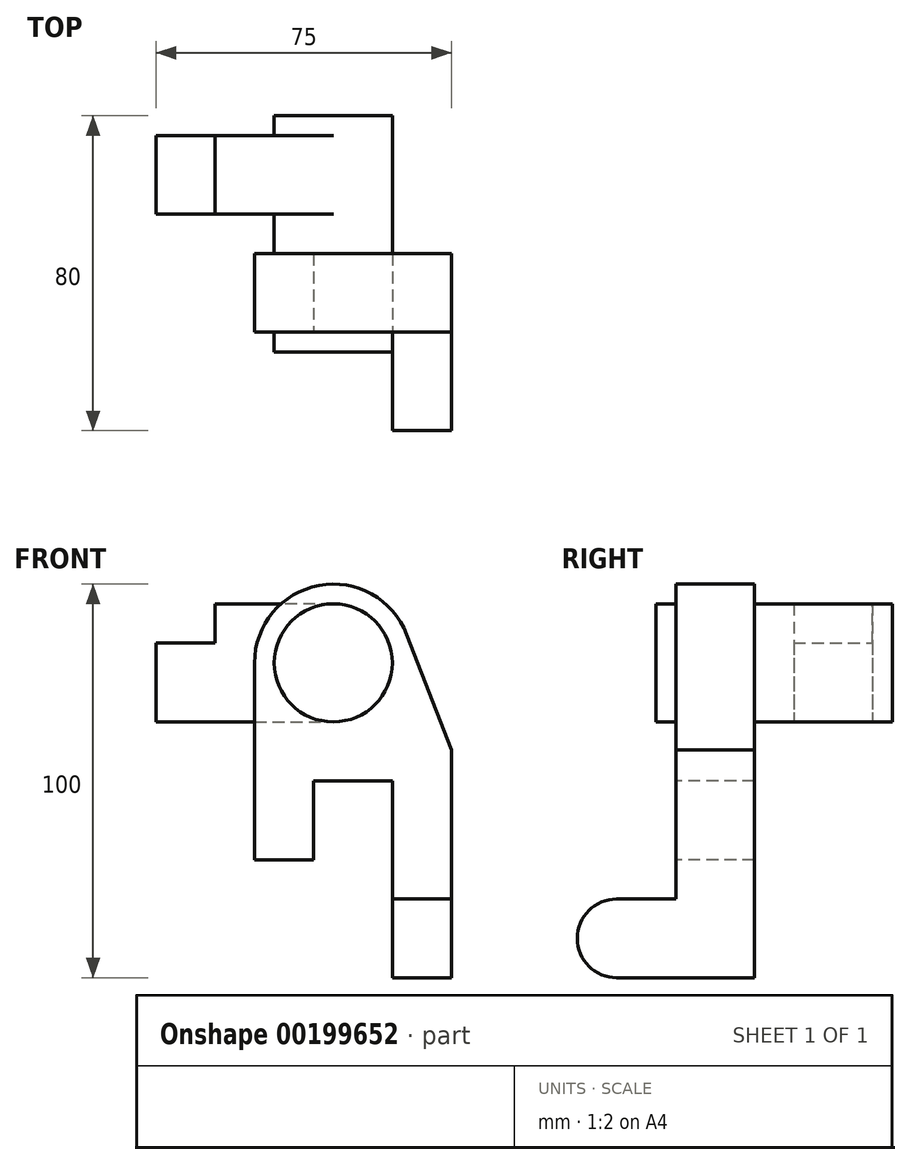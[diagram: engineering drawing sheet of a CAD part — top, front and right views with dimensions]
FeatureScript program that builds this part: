
annotation { "Feature Type Name" : "Feature", "Feature Type Description" : "" }
export const myFeature = defineFeature(function(context is Context, id is Id, definition is map)
    precondition{}
    {
        {
            var Q0;
            Q0=qCreatedBy(makeId("Front.planeOp"),FACE);
            var sketch = newSketch(context, id + "F0", { "sketchPlane" : qUnion([Q0])});
            skCircle(sketch, "E0", {"center": v(0, 0) * mm, "radius": 20 * mm});
            skLineSegment(sketch, "E1", {"start": v(-20, 0) * mm, "end": v(-20, -50) * mm});
            skLineSegment(sketch, "E2", {"start": v(-20, -50) * mm, "end": v(-5, -50) * mm});
            skLineSegment(sketch, "E3", {"start": v(-5, -50) * mm, "end": v(-5, -30) * mm});
            skLineSegment(sketch, "E4", {"start": v(-5, -30) * mm, "end": v(15, -30) * mm});
            skLineSegment(sketch, "E5", {"start": v(15, -30) * mm, "end": v(15, -80) * mm});
            skLineSegment(sketch, "E6", {"start": v(15, -80) * mm, "end": v(30, -80) * mm});
            skLineSegment(sketch, "E7", {"start": v(30, -80) * mm, "end": v(30, -22.08) * mm});
            skLineSegment(sketch, "E8", {"start": v(30, -22.08) * mm, "end": v(18.65, 7.22) * mm});
            skSolve(sketch);
        }
        {
            var Q0;
            {var subQ0=sQuery(id+"F0.wireOp",EDGE,"E1");Q0=makeQuery(id+"F0.imprint","IMPRINT",FACE,{"disambiguationData":[TD([[makeQuery(id+"F0.imprint","IMPRINT",EDGE,{"derivedFrom":subQ0}),1.0]])]});}
            var Q1;
            {var subQ0=sQuery(id+"F0.wireOp",EDGE,"E0");var subQ1=makeQuery(id+"F0.imprint","INTERSECT",VERTEX,{"derivedFrom":[subQ0,sQuery(id+"F0.wireOp",EDGE,"E1")]});Q1=makeQuery(id+"F0.imprint","IMPRINT",FACE,{"disambiguationData":[TD([[makeQuery(id+"F0.imprint","IMPRINT",EDGE,{"disambiguationData":[TD([[subQ1,1.0]])],"derivedFrom":subQ0}),1.0]])]});}
            extrude(context, id + "F1", {"entities" : qUnion([Q0, Q1]), "oppositeDirection" : true, "depth" : 20 * mm});
        }
        {
            var Q0;
            Q0=makeQuery(id+"F1.opExtrude","CAP_FACE",FACE,{"disambiguationData":[OSD([sQuery(id+"F0.wireOp",EDGE,"E0"),sQuery(id+"F0.wireOp",EDGE,"E1"),sQuery(id+"F0.wireOp",EDGE,"E2"),sQuery(id+"F0.wireOp",EDGE,"E3"),sQuery(id+"F0.wireOp",EDGE,"E4"),sQuery(id+"F0.wireOp",EDGE,"E5"),sQuery(id+"F0.wireOp",EDGE,"E6"),sQuery(id+"F0.wireOp",EDGE,"E7"),sQuery(id+"F0.wireOp",EDGE,"E8")])],"isStart":true});
            var sketch = newSketch(context, id + "F2", { "sketchPlane" : qUnion([Q0])});
            skCircle(sketch, "E9", {"center": v(0, 0) * mm, "radius": 15 * mm});
            skSolve(sketch);
        }
        {
            var Q0;
            Q0 = qSketchRegion(id + "F2", true);
            extrude(context, id + "F3", {"entities" : qUnion([Q0]), "operationType" : NewBodyOperationType.ADD, "depth" : 5 * mm, "hasSecondDirection" : true, "secondDirectionOppositeDirection" : true, "secondDirectionDepth" : 55 * mm});
        }
        {
            var Q0;
            Q0=makeQuery(id+"F1.opExtrude","CAP_FACE",FACE,{"disambiguationData":[OSD([sQuery(id+"F0.wireOp",EDGE,"E0"),sQuery(id+"F0.wireOp",EDGE,"E1"),sQuery(id+"F0.wireOp",EDGE,"E2"),sQuery(id+"F0.wireOp",EDGE,"E3"),sQuery(id+"F0.wireOp",EDGE,"E4"),sQuery(id+"F0.wireOp",EDGE,"E5"),sQuery(id+"F0.wireOp",EDGE,"E6"),sQuery(id+"F0.wireOp",EDGE,"E7"),sQuery(id+"F0.wireOp",EDGE,"E8")])],"isStart":true});
            var sketch = newSketch(context, id + "F4", { "sketchPlane" : qUnion([Q0])});
            skLineSegment(sketch, "E10.bottom", {"start": v(15, -80) * mm, "end": v(30, -80) * mm});
            skLineSegment(sketch, "E10.top", {"start": v(15, -60) * mm, "end": v(30, -60) * mm});
            skLineSegment(sketch, "E10.left", {"start": v(15, -80) * mm, "end": v(15, -60) * mm});
            skLineSegment(sketch, "E10.right", {"start": v(30, -80) * mm, "end": v(30, -60) * mm});
            skSolve(sketch);
        }
        {
            var Q0;
            Q0 = qSketchRegion(id + "F4", true);
            extrude(context, id + "F5", {"entities" : qUnion([Q0]), "operationType" : NewBodyOperationType.ADD, "depth" : 25 * mm});
        }
        {
            var Q0;
            Q0=makeQuery(id+"F5.opExtrude","CAP_EDGE",EDGE,{"disambiguationData":[OSD([sQuery(id+"F4.wireOp",EDGE,"E10.top")])],"isStart":false});
            var Q1;
            Q1=makeQuery(id+"F5.opExtrude","CAP_EDGE",EDGE,{"disambiguationData":[OSD([sQuery(id+"F4.wireOp",EDGE,"E10.bottom")])],"isStart":false});
            fillet(context, id + "F6", {"entities" : qUnion([Q0, Q1]), "radius" : 10 * mm, "tangentPropagation" : true, "allowEdgeOverflow" : false});
        }
        {
            var Q0;
            Q0=makeQuery(id+"F3.opExtrude","CAP_FACE",FACE,{"disambiguationData":[OSD([sQuery(id+"F2.wireOp",EDGE,"E9")])],"isStart":true});
            var sketch = newSketch(context, id + "F7", { "sketchPlane" : qUnion([Q0])});
            skLineSegment(sketch, "E11", {"start": v(0, 15) * mm, "end": v(45, 15) * mm});
            skLineSegment(sketch, "E12", {"start": v(45, 15) * mm, "end": v(45, -15) * mm});
            skLineSegment(sketch, "E13", {"start": v(45, -15) * mm, "end": v(0, -15) * mm});
            skLineSegment(sketch, "E14", {"start": v(30, 15) * mm, "end": v(30, 5) * mm});
            skLineSegment(sketch, "E15", {"start": v(30, 5) * mm, "end": v(45, 5) * mm});
            skSolve(sketch);
        }
        {
            var Q0;
            Q0 = qSketchRegion(id + "F7", true);
            var Q1;
            {var subQ1=sQuery(id+"F7.wireOp",EDGE,"E13");Q1=makeQuery(id+"F7.imprint","IMPRINT",FACE,{"disambiguationData":[TD([[makeQuery(id+"F7.imprint","IMPRINT",EDGE,{"derivedFrom":subQ1}),-1.0]])]});}
            extrude(context, id + "F8", {"entities" : qUnion([Q0, Q1]), "operationType" : NewBodyOperationType.ADD, "oppositeDirection" : true, "depth" : 25 * mm});
        }
        {
            var Q0;
            {var subQ3=sQuery(id+"F7.wireOp",EDGE,"E14");Q0=makeQuery(id+"F7.imprint","IMPRINT",FACE,{"disambiguationData":[TD([[makeQuery(id+"F7.imprint","IMPRINT",EDGE,{"derivedFrom":subQ3}),1.0]])]});}
            extrude(context, id + "F9", {"entities" : qUnion([Q0]), "operationType" : NewBodyOperationType.REMOVE, "oppositeDirection" : true, "depth" : 25 * mm});
        }
        {
            var Q0;
            Q0 = qSketchRegion(id + "F7", true);
            var Q1;
            {var subQ1=sQuery(id+"F7.wireOp",EDGE,"E13");Q1=makeQuery(id+"F7.imprint","IMPRINT",FACE,{"disambiguationData":[TD([[makeQuery(id+"F7.imprint","IMPRINT",EDGE,{"derivedFrom":subQ1}),-1.0]])]});}
            extrude(context, id + "F10", {"entities" : qUnion([Q0, Q1]), "operationType" : NewBodyOperationType.REMOVE, "oppositeDirection" : true, "depth" : 5 * mm});
        }
    });
